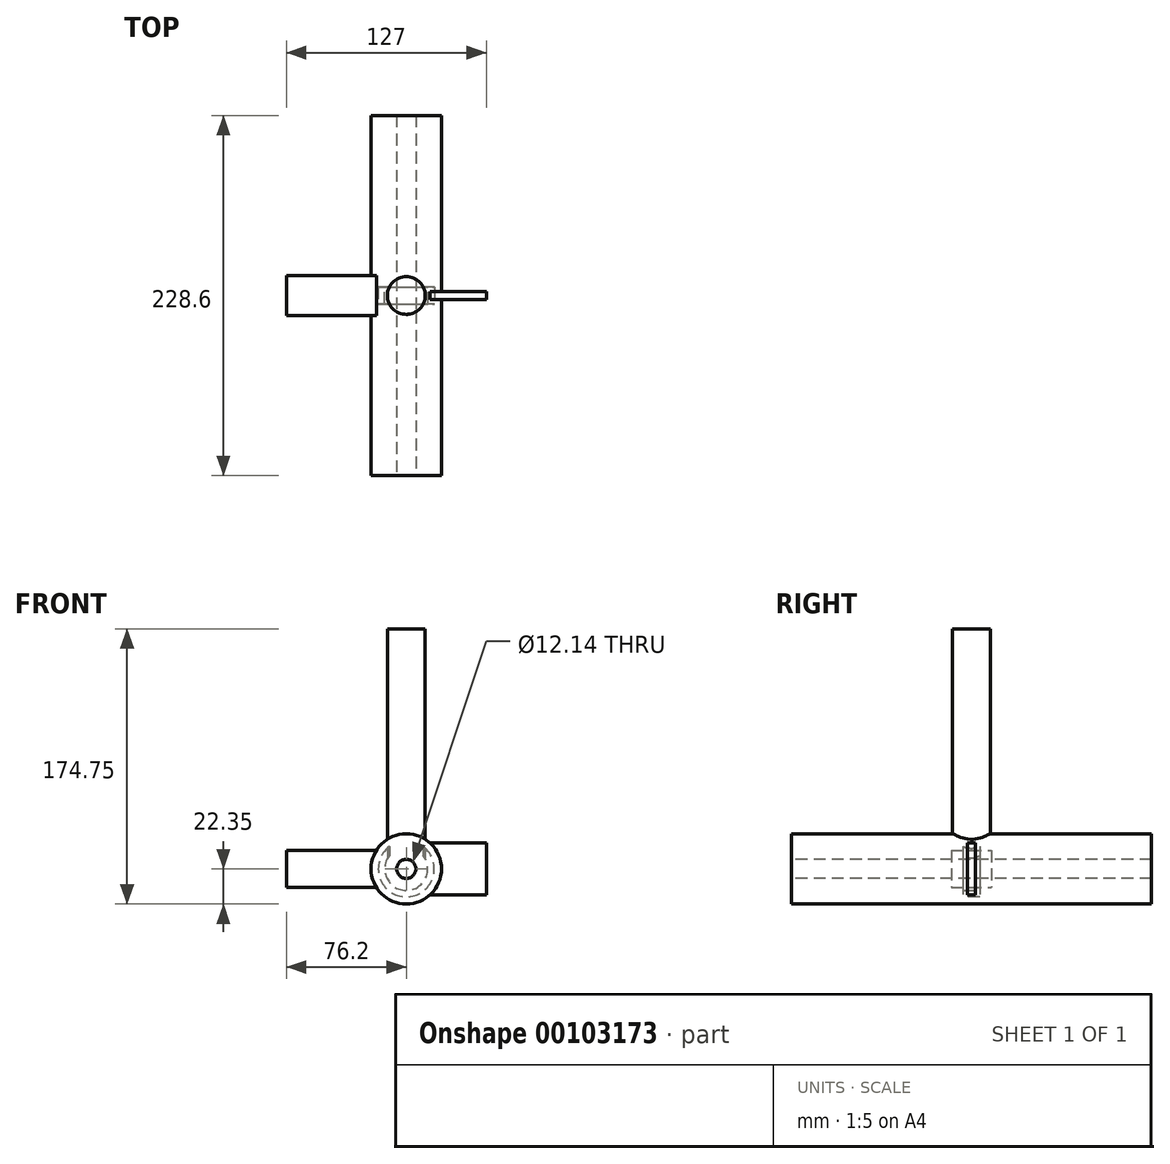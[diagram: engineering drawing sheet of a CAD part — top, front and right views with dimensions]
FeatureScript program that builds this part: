
annotation { "Feature Type Name" : "Feature", "Feature Type Description" : "" }
export const myFeature = defineFeature(function(context is Context, id is Id, definition is map)
    precondition{}
    {
        {
            var Q0;
            Q0=qCreatedBy(makeId("Front.planeOp"),FACE);
            var sketch = newSketch(context, id + "F0", { "sketchPlane" : qUnion([Q0])});
            skCircle(sketch, "E0", {"center": v(0, 0) * mm, "radius": 22.35 * mm});
            skSolve(sketch);
        }
        {
            var Q0;
            Q0=makeQuery(id+"F0.imprint","IMPRINT",FACE,{"disambiguationData":[TD([[makeQuery(id+"F0.imprint","IMPRINT",EDGE,{"derivedFrom":sQuery(id+"F0.wireOp",EDGE,"E0")}),1.0]])]});
            extrude(context, id + "F1", {"entities" : qUnion([Q0]), "endBound" : BoundingType.SYMMETRIC, "depth" : 228.6 * mm});
        }
        {
            var Q0;
            Q0=qCreatedBy(makeId("Front.planeOp"),FACE);
            var sketch = newSketch(context, id + "F2", { "sketchPlane" : qUnion([Q0])});
            skCircle(sketch, "E1", {"center": v(0, 0) * mm, "radius": 4.95 * mm});
            skSolve(sketch);
        }
        {
            var Q0;
            Q0 = qSketchRegion(id + "F2", true);
            extrude(context, id + "F3", {"entities" : qUnion([Q0]), "endBound" : BoundingType.SYMMETRIC, "depth" : 101.6 * mm});
        }
        {
            var Q0;
            Q0=qCreatedBy(makeId("Front.planeOp"),FACE);
            var sketch = newSketch(context, id + "F4", { "sketchPlane" : qUnion([Q0])});
            skCircle(sketch, "E2", {"center": v(0, 0) * mm, "radius": 5.94 * mm});
            skSolve(sketch);
        }
        {
            var Q0;
            Q0 = qSketchRegion(id + "F4", true);
            extrude(context, id + "F5", {"entities" : qUnion([Q0]), "endBound" : BoundingType.SYMMETRIC, "depth" : 101.6 * mm});
        }
        {
            var Q0;
            Q0=qCreatedBy(makeId("Front.planeOp"),FACE);
            var sketch = newSketch(context, id + "F6", { "sketchPlane" : qUnion([Q0])});
            skCircle(sketch, "E3", {"center": v(0, 0) * mm, "radius": 16.51 * mm});
            skLineSegment(sketch, "E4", {"start": v(0, 16.51) * mm, "end": v(50.8, 16.51) * mm});
            skLineSegment(sketch, "E5", {"start": v(50.8, 16.51) * mm, "end": v(50.8, -16.5) * mm});
            skLineSegment(sketch, "E6", {"start": v(50.8, -16.5) * mm, "end": v(0, -16.51) * mm});
            skCircle(sketch, "E7", {"center": v(0, 0) * mm, "radius": 5.08 * mm});
            skSolve(sketch);
        }
        {
            var Q0;
            Q0=makeQuery(id+"F6.imprint","IMPRINT",FACE,{"disambiguationData":[TD([[makeQuery(id+"F6.imprint","IMPRINT",EDGE,{"derivedFrom":sQuery(id+"F6.wireOp",EDGE,"E7")}),-1.0]])]});
            var Q1;
            {var subQ0=sQuery(id+"F6.wireOp",EDGE,"E4");Q1=makeQuery(id+"F6.imprint","IMPRINT",FACE,{"disambiguationData":[TD([[makeQuery(id+"F6.imprint","IMPRINT",EDGE,{"derivedFrom":subQ0}),-1.0]])]});}
            extrude(context, id + "F7", {"entities" : qUnion([Q0, Q1]), "endBound" : BoundingType.SYMMETRIC, "depth" : 4.88 * mm});
        }
        {
            var Q0;
            Q0=qCreatedBy(makeId("Front.planeOp"),FACE);
            var sketch = newSketch(context, id + "F8", { "sketchPlane" : qUnion([Q0])});
            skCircle(sketch, "E8", {"center": v(0, 0) * mm, "radius": 11.78 * mm});
            skLineSegment(sketch, "E9", {"start": v(0, 11.78) * mm, "end": v(-76.2, 11.78) * mm});
            skLineSegment(sketch, "E10", {"start": v(-76.2, 11.78) * mm, "end": v(-76.2, -11.78) * mm});
            skLineSegment(sketch, "E11", {"start": v(-76.2, -11.78) * mm, "end": v(0, -11.78) * mm});
            skCircle(sketch, "E12", {"center": v(0, 0) * mm, "radius": 5.08 * mm});
            skSolve(sketch);
        }
        {
            var Q0;
            {var subQ0=sQuery(id+"F8.wireOp",EDGE,"E9");Q0=makeQuery(id+"F8.imprint","IMPRINT",FACE,{"disambiguationData":[TD([[makeQuery(id+"F8.imprint","IMPRINT",EDGE,{"derivedFrom":subQ0}),1.0]])]});}
            var Q1;
            Q1=makeQuery(id+"F8.imprint","IMPRINT",FACE,{"disambiguationData":[TD([[makeQuery(id+"F8.imprint","IMPRINT",EDGE,{"derivedFrom":sQuery(id+"F8.wireOp",EDGE,"E12")}),-1.0]])]});
            extrude(context, id + "F9", {"entities" : qUnion([Q0, Q1]), "endBound" : BoundingType.SYMMETRIC, "depth" : 25.4 * mm});
        }
        {
            var Q0;
            Q0=qCreatedBy(makeId("Front.planeOp"),FACE);
            var sketch = newSketch(context, id + "F10", { "sketchPlane" : qUnion([Q0])});
            skCircle(sketch, "E13", {"center": v(0, 0) * mm, "radius": 17.78 * mm});
            skSolve(sketch);
        }
        {
            var Q0;
            Q0=makeQuery(id+"F10.imprint","IMPRINT",FACE,{"disambiguationData":[TD([[makeQuery(id+"F10.imprint","IMPRINT",EDGE,{"derivedFrom":sQuery(id+"F10.wireOp",EDGE,"E13")}),1.0]])]});
            extrude(context, id + "F11", {"entities" : qUnion([Q0]), "operationType" : NewBodyOperationType.REMOVE, "endBound" : BoundingType.SYMMETRIC, "oppositeDirection" : true, "depth" : 10.67 * mm});
        }
        {
            var Q0;
            Q0=qCreatedBy(makeId("Front.planeOp"),FACE);
            var sketch = newSketch(context, id + "F12", { "sketchPlane" : qUnion([Q0])});
            skCircle(sketch, "E14", {"center": v(0, 0) * mm, "radius": 13.66 * mm});
            skSolve(sketch);
        }
        {
            var Q0;
            Q0 = qSketchRegion(id + "F12", true);
            extrude(context, id + "F13", {"entities" : qUnion([Q0]), "endBound" : BoundingType.SYMMETRIC, "depth" : 43.18 * mm});
        }
        {
            var Q0;
            Q0=qCreatedBy(makeId("Top.planeOp"),FACE);
            var sketch = newSketch(context, id + "F14", { "sketchPlane" : qUnion([Q0])});
            skCircle(sketch, "E15", {"center": v(0, 0) * mm, "radius": 12 * mm});
            skSolve(sketch);
        }
        {
            var Q0;
            Q0 = qSketchRegion(id + "F14", true);
            extrude(context, id + "F15", {"entities" : qUnion([Q0]), "operationType" : NewBodyOperationType.ADD, "depth" : 152.4 * mm});
        }
        {
            var Q0;
            Q0=qCreatedBy(makeId("Front.planeOp"),FACE);
            var sketch = newSketch(context, id + "F16", { "sketchPlane" : qUnion([Q0])});
            skCircle(sketch, "E16", {"center": v(0, 0) * mm, "radius": 6.07 * mm});
            skSolve(sketch);
        }
        {
            var Q0;
            Q0 = qSketchRegion(id + "F16", true);
            extrude(context, id + "F17", {"entities" : qUnion([Q0]), "operationType" : NewBodyOperationType.REMOVE, "endBound" : BoundingType.SYMMETRIC, "oppositeDirection" : true, "depth" : 254 * mm});
        }
    });
